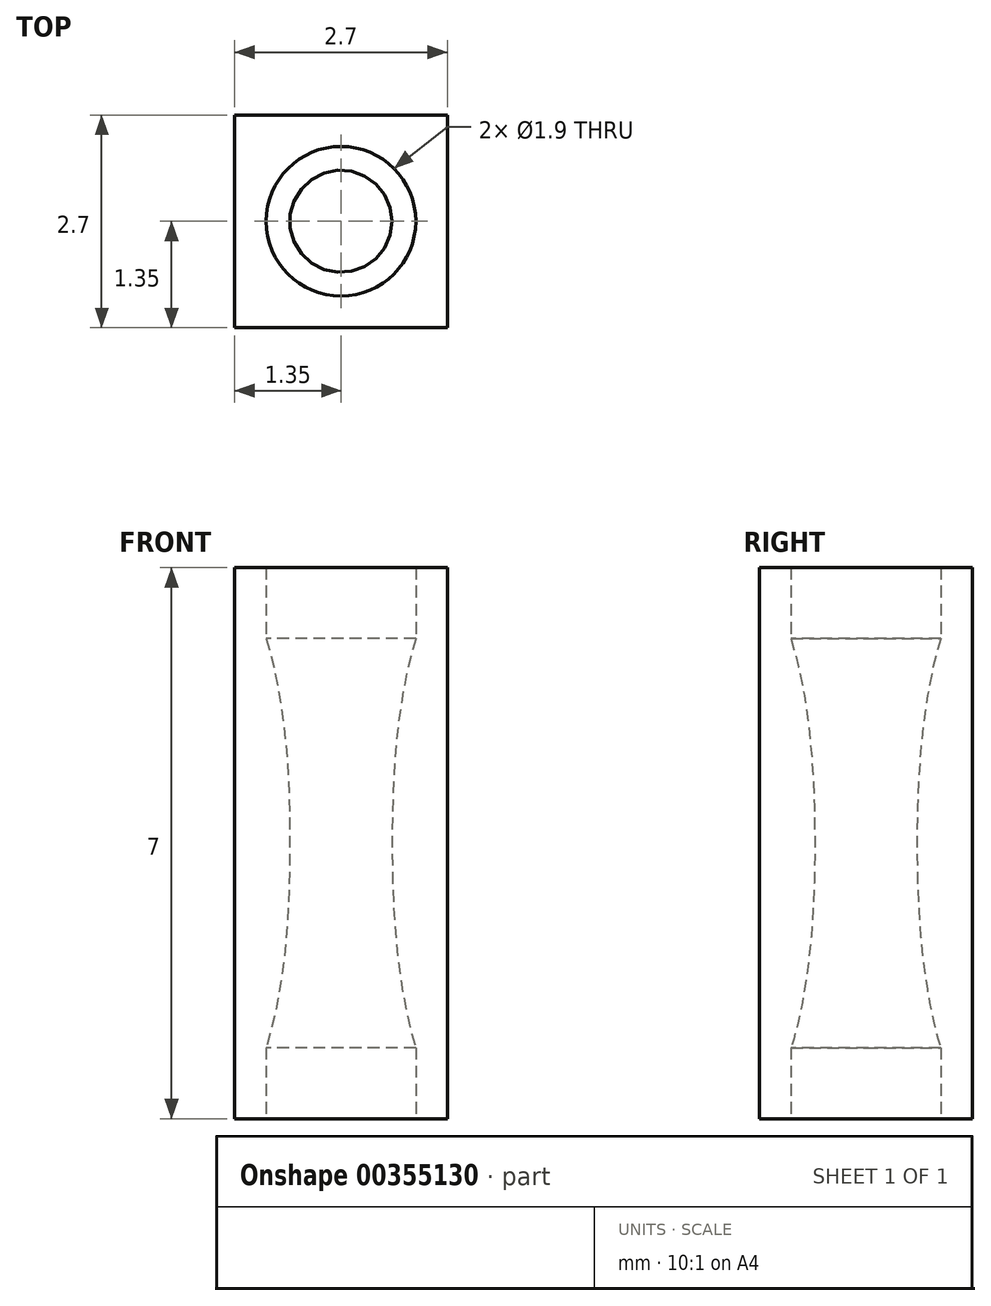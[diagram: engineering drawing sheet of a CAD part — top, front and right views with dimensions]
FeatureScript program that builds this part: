
annotation { "Feature Type Name" : "Feature", "Feature Type Description" : "" }
export const myFeature = defineFeature(function(context is Context, id is Id, definition is map)
    precondition{}
    {
        {
            var Q0;
            Q0=qCreatedBy(makeId("Front.planeOp"),FACE);
            var sketch = newSketch(context, id + "F0", { "sketchPlane" : qUnion([Q0])});
            skLineSegment(sketch, "E0", {"start": v(0, 3.5) * mm, "end": v(0, -3.5) * mm, "construction": true});
            skLineSegment(sketch, "E1", {"start": v(-1.35, 3.5) * mm, "end": v(-1.35, -3.5) * mm});
            skFitSpline(sketch, "E2", {"points": [v(-1.35, 3.5) * mm, v(-0.65, 0) * mm, v(-1.35, -3.5) * mm], "startDerivative": vector(3.48, -5.6) * mm, "endDerivative": vector(-3.48, -5.6) * mm});
            skLineSegment(sketch, "E3", {"start": v(-0.65, -3.5) * mm, "end": v(-0.65, 0) * mm, "construction": true});
            skLineSegment(sketch, "E4", {"start": v(-0.65, 0) * mm, "end": v(-0.65, 3.5) * mm, "construction": true});
            skSolve(sketch);
        }
        {
            var Q0;
            Q0=makeQuery(id+"F0.imprint","IMPRINT",FACE,{"disambiguationData":[TD([[makeQuery(id+"F0.imprint","IMPRINT",EDGE,{"derivedFrom":sQuery(id+"F0.wireOp",EDGE,"E1")}),1.0]])]});
            var Q1;
            Q1=sQuery(id+"F0.wireOp",EDGE,"E0");
            revolve(context, id + "F1", {"entities" : qUnion([Q0]), "axis" : qUnion([Q1]), "revolveType" : RevolveType.FULL});
        }
        {
            var Q0;
            Q0=qCreatedBy(makeId("Top.planeOp"),FACE);
            var sketch = newSketch(context, id + "F2", { "sketchPlane" : qUnion([Q0])});
            skLineSegment(sketch, "E5.bottom", {"start": v(1.35, 1.35) * mm, "end": v(-1.35, 1.35) * mm});
            skLineSegment(sketch, "E5.top", {"start": v(1.35, -1.35) * mm, "end": v(-1.35, -1.35) * mm});
            skLineSegment(sketch, "E5.left", {"start": v(1.35, 1.35) * mm, "end": v(1.35, -1.35) * mm});
            skLineSegment(sketch, "E5.right", {"start": v(-1.35, 1.35) * mm, "end": v(-1.35, -1.35) * mm});
            skPoint(sketch, "E5.middle", {"position": v(0, 0) * mm});
            skCircle(sketch, "E6", {"center": v(0, 0) * mm, "radius": 0.95 * mm});
            skSolve(sketch);
        }
        {
            var Q0;
            Q0=makeQuery(id+"F2.imprint","IMPRINT",FACE,{"disambiguationData":[TD([[makeQuery(id+"F2.imprint","IMPRINT",EDGE,{"derivedFrom":sQuery(id+"F2.wireOp",EDGE,"E5.bottom")}),1.0]])]});
            extrude(context, id + "F3", {"entities" : qUnion([Q0]), "operationType" : NewBodyOperationType.ADD, "endBound" : BoundingType.SYMMETRIC, "depth" : 7 * mm});
        }
    });
